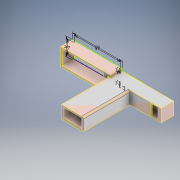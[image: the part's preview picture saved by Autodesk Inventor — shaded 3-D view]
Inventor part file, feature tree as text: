
AUTODESK INVENTOR PART (.ipt)
format: ipt  version: 2020 (Build 240168000, 168)  size: 467,456 bytes
history: native  units: mm
features: extrude x28, sketch x26, pattern_linear x3, other x2, chamfer x1, fillet x1
ambient origin geometry x8: Origin, YZ Plane, XZ Plane, XY Plane, X Axis, Y Axis, Z Axis, Center Point
bodies: Solid1 (feature_tree)
feature tree (61):
  extrude  "Extrusion1"  Depth=11.0mm
  extrude  "Extrusion2"  Depth=15.0mm
  sketch  "Sketch3"  dims[d4=70.0mm d5=0.0mm d7=1.0mm]
  extrude  "Extrusion3"  Depth=1.0mm
  sketch  "Sketch4"  dims[d8=1.0mm d9=6.0mm]
  extrude  "Extrusion4"  Depth=6.0mm
  extrude  "Extrusion5"  Depth=1.0mm
  extrude  "Extrusion6"  Depth=55.0mm
  extrude  "Extrusion7"  Depth=21.0mm
  extrude  "Extrusion8"  Depth=4.0mm
  extrude  "Extrusion9"  Depth=14.0mm TaperAngle=0.0deg
  extrude  "Extrusion10"  Depth=3.5mm
  extrude  "Extrusion11"  Depth=14.0mm TaperAngle=0.0deg
  extrude  "Extrusion12"  Depth=11.0mm
  extrude  "Extrusion13"  Depth=22.0mm TaperAngle=0.0deg
  extrude  "Extrusion14"  Depth=7.0mm
  extrude  "Extrusion15"  Depth=3.0mm
  extrude  "Extrusion16"  Depth=11.0mm TaperAngle=0.0deg
  extrude  "Extrusion17"  Depth=2.0mm
  extrude  "Extrusion18"  Depth=2.0mm
  extrude  "Extrusion19"  Depth=2.0mm TaperAngle=0.0deg
  extrude  "Extrusion20"  Depth=2.0mm
  extrude  "Extrusion21"  Depth=7.0mm TaperAngle=0.0deg
  extrude  "Extrusion22"  Depth=7.0mm TaperAngle=0.0deg
  extrude  "Extrusion23"  Depth=10.0mm
  pattern_linear  "Rectangular Pattern1"  Spacing1=13.0mm  [1 undecoded]
  pattern_linear  "Rectangular Pattern2"  Spacing1=2.0mm  [1 undecoded]
  extrude  "Extrusion24"  Depth=2.0mm TaperAngle=0.0deg
  pattern_linear  "Rectangular Pattern3"  Spacing1=2.0mm  [1 undecoded]
  extrude  "Extrusion25"  Depth=5.0mm TaperAngle=0.0deg
  extrude  "Extrusion27"  Depth=0.5mm
  chamfer  "Chamfer1"  Distance=2.0mm
  extrude  "Extrusion29"  Depth=30.0mm
  fillet  "Fillet1"  Radius=30.0mm
  extrude  "Extrusion30"  Depth=0.5mm
  sketch  "Sketch1"  dims[d0=22.0mm d1=11.0mm]
  sketch  "Sketch2"  dims[d2=26.0mm d3=15.0mm]
  sketch  "Sketch5"  dims[d10=2.0mm d11=0.0mm d12=1.0mm]
  sketch  "Sketch6"  dims[d14=17.0mm d15=55.0mm]
  sketch  "Sketch7"  dims[d19=3.0mm d21=21.0mm]
  sketch  "Sketch8"  dims[d22=59.0mm d23=4.0mm]
  sketch  "Sketch9"  dims[d24=6.0mm d25=14.0mm d26=0.0mm]
  sketch  "Sketch10"  dims[d27=3.5mm d28=0.0mm d29=3.5mm]
  sketch  "Sketch11"  dims[d30=3.5mm d31=14.0mm d32=0.0mm]
  sketch  "Sketch12"  dims[d33=14.0mm d34=0.0mm d39=11.0mm]
  sketch  "Sketch13"  dims[d40=2.0mm d41=22.0mm d42=0.0mm]
  sketch  "Sketch14"  dims[d45=2.0mm d46=7.0mm]
  sketch  "Sketch15"  dims[d48=2.0mm d49=0.0mm d50=3.0mm]
  sketch  "Sketch16"  dims[d51=1.5mm d52=11.0mm d53=0.0mm]
  sketch  "Sketch17"  dims[d58=37.0mm d59=0.0mm d60=2.0mm]
  sketch  "Sketch18"  dims[d61=13.0mm d62=0.0mm d63=2.0mm]
  sketch  "Sketch19"  dims[d64=2.0mm d65=83.0mm d66=0.0mm]
  sketch  "Sketch20"  dims[d67=42.0mm d68=0.0mm d70=2.0mm]
  sketch  "Sketch21"  dims[d71=15.0mm d72=0.0mm d73=7.0mm d74=0.0mm]
  sketch  "Sketch22"  dims[d75=2.0mm d76=7.0mm d77=0.0mm]
  sketch  "Sketch23"  dims[d78=5.0mm d79=0.0mm d80=10.0mm]
  sketch  "Sketch25"  dims[d81=10.0mm]
  sketch  "Sketch28"  dims[d82=2.0mm d83=0.0mm]
  sketch  "Sketch29"  dims[d84=2.0mm d85=13.0mm d86=2.0mm d87=0.0mm d88=2.0mm d89=0.0mm d90=2.0mm d91=0.0mm d92=5.0mm d93=0.0mm d96=2.4mm d97=2.0mm d98=0.0mm d99=20.0mm d101=30.0mm d102=30.0mm d104=25.0mm d107=2.4mm d108=2.0mm d109=0.0mm d110=20.0mm d112=20.0mm d113=30.0mm d115=30.0mm d116=35.0mm d117=0.0mm d120=25.0mm d121=0.0mm d122=2.0mm d123=2.0mm d124=45.0deg d128=10.0mm d129=0.0mm d130=2.0mm d131=7.5mm d132=2.0mm d133=0.0mm d35=0.5mm d36=0.872665mm d69=0.5mm]
  other  "Composite1"
  other  "Srf1"
note: 3 required parameter values undecoded (feature->parameter linkage not recoverable at this tier; creation-order binding heuristic only, values carry confidence <= 0.55)
